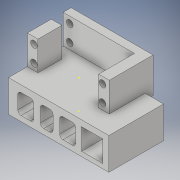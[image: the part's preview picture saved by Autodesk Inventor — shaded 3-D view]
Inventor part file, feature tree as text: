
AUTODESK INVENTOR PART (.ipt)
format: ipt  version: 2018 (Build 220112000, 112)  size: 348,672 bytes
history: native  units: in
note: dims shown in document units (in); Inventor stores cm internally (conversion verified against a paired STEP export)
features: sketch x21, extrude x16, fillet x9, hole x1
ambient origin geometry x8: Origin, YZ Plane, XZ Plane, XY Plane, X Axis, Y Axis, Z Axis, Center Point
bodies: Solid1 (feature_tree)
feature tree (47):
  extrude  "Extrusion1"  Depth=2.06in
  extrude  "Extrusion2"  Depth=0.25in
  extrude  "Extrusion3"  Depth=0.25in
  sketch  "Sketch4"  dims[d7=0.25in d8=0.75in d9=0.0in]
  extrude  "Extrusion4"  Depth=0.75in TaperAngle=0.0deg
  sketch  "Sketch6"  dims[d13=0.3in d14=2.285in]
  extrude  "Extrusion5"  Depth=0.3in
  extrude  "Extrusion6"  Depth=2.285in
  extrude  "Extrusion7"  Depth=0.71in
  extrude  "Extrusion8"  Depth=0.45in
  fillet  "Fillet1"  Radius=1.1in
  sketch  "Sketch11"  dims[d30=0.15in d31=0.2in]
  hole  "Hole1"  [1 undecoded]
  extrude  "Extrusion9"  Depth=0.125in
  extrude  "Extrusion10"  Depth=0.2in
  sketch  "Sketch15"  dims[d53=0.25in d54=0.4767in]
  extrude  "Extrusion11"  Depth=0.2in
  fillet  "Fillet2"  Radius=0.24in
  fillet  "Fillet3"  Radius=0.2in
  fillet  "Fillet4"  Radius=0.24in
  fillet  "Fillet5"  Radius=0.15in
  fillet  "Fillet6"  Radius=0.2in
  fillet  "Fillet7"  Radius=0.15in
  fillet  "Fillet8"  Radius=0.24in
  fillet  "Fillet9"  Radius=0.1in
  extrude  "Extrusion12"  Depth=0.25in
  extrude  "Extrusion13"  Depth=0.4767in
  extrude  "Extrusion14"  Depth=1.0in TaperAngle=0.0deg
  extrude  "Extrusion15"  Depth=0.125in
  extrude  "Extrusion16"  Depth=0.125in
  sketch  "Sketch1"  dims[d0=2.06in d1=3.68in]
  sketch  "Sketch2"  dims[d2=0.2in d3=0.0in d4=0.25in]
  sketch  "Sketch3"  dims[d5=0.75in d6=0.25in]
  sketch  "Sketch5"  dims[d10=0.25in d11=0.0in d12=0.3in]
  sketch  "Sketch7"  dims[d15=1.1in d16=0.0in d17=0.71in]
  sketch  "Sketch8"  dims[d18=1.1in d19=0.0in d20=0.45in d21=1.1in d22=0.0in]
  sketch  "Sketch9"  dims[d23=0.3in d24=0.0in d25=1.1in d26=0.0in]
  sketch  "Sketch10"  dims[d27=0.125in d29=0.24in]
  sketch  "Sketch12"  dims[d32=0.2in d33=0.15in d34=0.24in d35=0.2in d36=0.24in d37=0.15in d38=0.2in d39=0.15in d40=0.24in]
  sketch  "Sketch13"  dims[d41=0.25in d42=0.75in d43=0.375in d44=0.25in d45=0.5635in d46=1.0in d47=0.8108in d48=0.1in d49=0.0in]
  sketch  "Sketch14"  dims[d50=0.1in d51=0.0in d52=0.25in]
  sketch  "Sketch16"  dims[d55=0.4767in d56=1.0in d57=0.0in]
  sketch  "Sketch17"  dims[d58=0.125in d59=0.125in]
  sketch  "Sketch18"  dims[d60=0.125in d61=0.125in]
  sketch  "Sketch19"  dims[d62=0.125in]
  sketch  "Sketch20"  dims[d63=0.125in]
  sketch  "Sketch21"  dims[d64=0.125in d65=0.125in d66=0.025in d67=0.0in d68=0.025in d69=0.0in d70=0.025in d71=0.0in d72=0.025in d73=0.0in d74=0.025in d75=0.0in]
note: 1 required parameter value undecoded (feature->parameter linkage not recoverable at this tier; creation-order binding heuristic only, values carry confidence <= 0.55)
